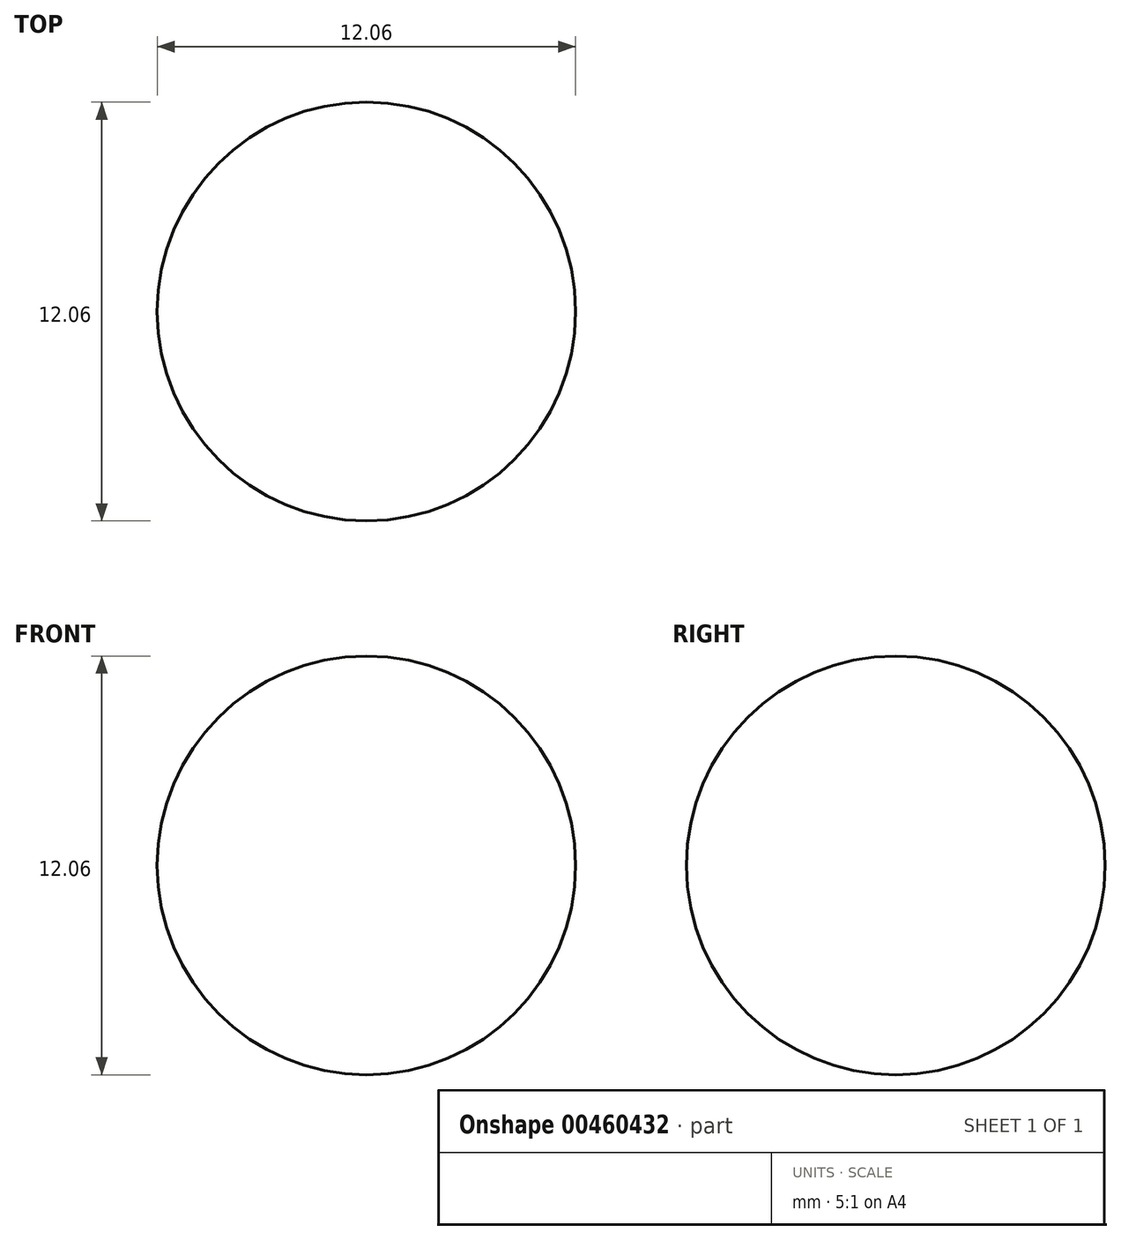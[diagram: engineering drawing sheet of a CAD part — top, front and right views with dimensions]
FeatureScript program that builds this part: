
annotation { "Feature Type Name" : "Feature", "Feature Type Description" : "" }
export const myFeature = defineFeature(function(context is Context, id is Id, definition is map)
    precondition{}
    {
        {
            var Q0;
            Q0=qCreatedBy(makeId("Top.planeOp"),FACE);
            var sketch = newSketch(context, id + "F0", { "sketchPlane" : qUnion([Q0])});
            skCircle(sketch, "E0", {"center": v(0, 0) * mm, "radius": 6.03 * mm});
            skLineSegment(sketch, "E1", {"start": v(-6.03, 0) * mm, "end": v(6.03, 0) * mm});
            skSolve(sketch);
        }
        {
            var Q0;
            {var subQ0=sQuery(id+"F0.wireOp",EDGE,"E1");Q0=makeQuery(id+"F0.imprint","IMPRINT",FACE,{"disambiguationData":[TD([[makeQuery(id+"F0.imprint","IMPRINT",EDGE,{"derivedFrom":subQ0}),1.0]])]});}
            var Q1;
            Q1=sQuery(id+"F0.wireOp",EDGE,"E1");
            revolve(context, id + "F1", {"surfaceOperationType" : NewSurfaceOperationType.NEW, "entities" : qUnion([Q0]), "axis" : qUnion([Q1]), "revolveType" : RevolveType.FULL});
        }
    });
